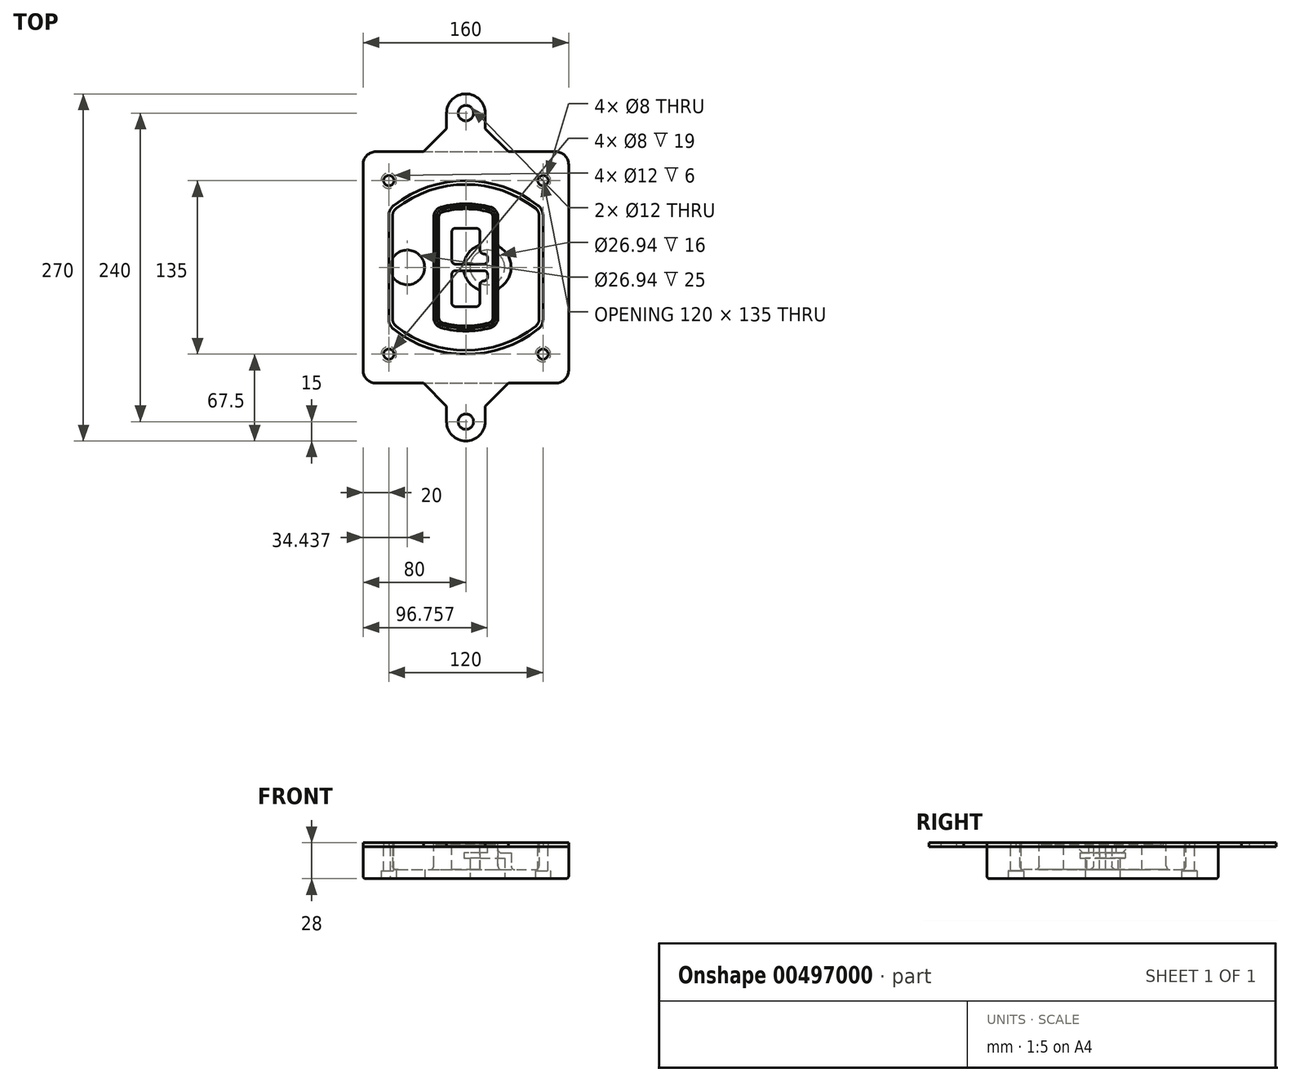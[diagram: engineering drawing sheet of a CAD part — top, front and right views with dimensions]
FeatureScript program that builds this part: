
annotation { "Feature Type Name" : "Feature", "Feature Type Description" : "" }
export const myFeature = defineFeature(function(context is Context, id is Id, definition is map)
    precondition{}
    {
        {
            var Q0;
            Q0=qCreatedBy(makeId("Top.planeOp"),FACE);
            var sketch = newSketch(context, id + "F0", { "sketchPlane" : qUnion([Q0])});
            skPoint(sketch, "E0.rect.middle", {"position": v(0, 0) * mm});
            skLineSegment(sketch, "E1.bottom", {"start": v(-70, -90) * mm, "end": v(70, -90) * mm});
            skLineSegment(sketch, "E1.top", {"start": v(-70, 90) * mm, "end": v(70, 90) * mm});
            skLineSegment(sketch, "E1.left", {"start": v(-80, -80) * mm, "end": v(-80, 80) * mm});
            skLineSegment(sketch, "E1.right", {"start": v(80, -80) * mm, "end": v(80, 80) * mm});
            skLineSegment(sketch, "E2", {"start": v(-80, 90) * mm, "end": v(80, -90) * mm, "construction": true});
            skLineSegment(sketch, "E3", {"start": v(80, 90) * mm, "end": v(-80, -90) * mm, "construction": true});
            skCircle(sketch, "E4", {"center": v(-60, 67.5) * mm, "radius": 4 * mm});
            skCircle(sketch, "E5", {"center": v(60, 67.5) * mm, "radius": 4 * mm});
            skCircle(sketch, "E6", {"center": v(60, -67.5) * mm, "radius": 4 * mm});
            skCircle(sketch, "E7", {"center": v(-60, -67.5) * mm, "radius": 4 * mm});
            skLineSegment(sketch, "E8", {"start": v(-60, 67.5) * mm, "end": v(60, 67.5) * mm, "construction": true});
            skLineSegment(sketch, "E9", {"start": v(60, 67.5) * mm, "end": v(60, -67.5) * mm, "construction": true});
            skLineSegment(sketch, "E10", {"start": v(60, -67.5) * mm, "end": v(-60, -67.5) * mm, "construction": true});
            skLineSegment(sketch, "E11", {"start": v(-60, -67.5) * mm, "end": v(-60, 67.5) * mm, "construction": true});
            skLineSegment(sketch, "E12", {"start": v(-60, 40.3) * mm, "end": v(-60, -40.3) * mm});
            skLineSegment(sketch, "E13", {"start": v(60, 40.3) * mm, "end": v(60, -40.3) * mm});
            skArc(sketch, "E14", {"start": v(56.15, 48.18) * mm, "mid": v(0, 67.5) * mm, "end": v(-56.15, 48.18) * mm});
            skArc(sketch, "E15", {"start": v(-56.15, -48.18) * mm, "mid": v(0, -67.5) * mm, "end": v(56.15, -48.18) * mm});
            skLineSegment(sketch, "E16", {"start": v(-60, 0) * mm, "end": v(60, 0) * mm, "construction": true});
            skPoint(sketch, "E17.visualSharp", {"position": v(-60, -45) * mm});
            skArc(sketch, "E17.filletArc", {"start": v(-60, -40.3) * mm, "mid": v(-58.99, -44.68) * mm, "end": v(-56.15, -48.18) * mm});
            skPoint(sketch, "E18.visualSharp", {"position": v(-60, 45) * mm});
            skArc(sketch, "E18.filletArc", {"start": v(-56.15, 48.18) * mm, "mid": v(-58.99, 44.68) * mm, "end": v(-60, 40.3) * mm});
            skPoint(sketch, "E19.visualSharp", {"position": v(60, 45) * mm});
            skArc(sketch, "E19.filletArc", {"start": v(60, 40.3) * mm, "mid": v(58.99, 44.68) * mm, "end": v(56.15, 48.18) * mm});
            skPoint(sketch, "E20.visualSharp", {"position": v(60, -45) * mm});
            skArc(sketch, "E20.filletArc", {"start": v(56.15, -48.18) * mm, "mid": v(58.99, -44.68) * mm, "end": v(60, -40.3) * mm});
            skPoint(sketch, "E21.visualSharp", {"position": v(-80, 90) * mm});
            skArc(sketch, "E21.filletArc", {"start": v(-70, 90) * mm, "mid": v(-77.07, 87.07) * mm, "end": v(-80, 80) * mm});
            skPoint(sketch, "E22.visualSharp", {"position": v(80, 90) * mm});
            skArc(sketch, "E22.filletArc", {"start": v(80, 80) * mm, "mid": v(77.07, 87.07) * mm, "end": v(70, 90) * mm});
            skPoint(sketch, "E23.visualSharp", {"position": v(80, -90) * mm});
            skArc(sketch, "E23.filletArc", {"start": v(70, -90) * mm, "mid": v(77.07, -87.07) * mm, "end": v(80, -80) * mm});
            skPoint(sketch, "E24.visualSharp", {"position": v(-80, -90) * mm});
            skArc(sketch, "E24.filletArc", {"start": v(-80, -80) * mm, "mid": v(-77.07, -87.07) * mm, "end": v(-70, -90) * mm});
            skArc(sketch, "E25.0", {"start": v(57, 40.3) * mm, "mid": v(56.3, 43.36) * mm, "end": v(54.3, 45.81) * mm});
            skLineSegment(sketch, "E25.1", {"start": v(57, 40.3) * mm, "end": v(57, -40.3) * mm});
            skArc(sketch, "E25.2", {"start": v(54.3, -45.81) * mm, "mid": v(56.3, -43.36) * mm, "end": v(57, -40.3) * mm});
            skArc(sketch, "E25.3", {"start": v(-54.3, -45.81) * mm, "mid": v(0, -64.5) * mm, "end": v(54.3, -45.81) * mm});
            skArc(sketch, "E25.4", {"start": v(-57, -40.3) * mm, "mid": v(-56.3, -43.36) * mm, "end": v(-54.3, -45.81) * mm});
            skArc(sketch, "E25.5", {"start": v(54.3, 45.81) * mm, "mid": v(0, 64.5) * mm, "end": v(-54.3, 45.81) * mm});
            skLineSegment(sketch, "E25.6", {"start": v(-57, 40.3) * mm, "end": v(-57, -40.3) * mm});
            skArc(sketch, "E25.7", {"start": v(-54.3, 45.81) * mm, "mid": v(-56.3, 43.36) * mm, "end": v(-57, 40.3) * mm});
            skArc(sketch, "E26.0", {"start": v(-58.62, 51.33) * mm, "mid": v(-62.58, 46.43) * mm, "end": v(-64, 40.3) * mm});
            skArc(sketch, "E26.1", {"start": v(58.62, 51.33) * mm, "mid": v(0, 71.5) * mm, "end": v(-58.62, 51.33) * mm});
            skArc(sketch, "E26.2", {"start": v(64, 40.3) * mm, "mid": v(62.58, 46.43) * mm, "end": v(58.62, 51.33) * mm});
            skLineSegment(sketch, "E26.3", {"start": v(64, 40.3) * mm, "end": v(64, -40.3) * mm});
            skArc(sketch, "E26.4", {"start": v(58.62, -51.33) * mm, "mid": v(62.58, -46.43) * mm, "end": v(64, -40.3) * mm});
            skLineSegment(sketch, "E26.5", {"start": v(-64, 40.3) * mm, "end": v(-64, -40.3) * mm});
            skArc(sketch, "E26.6", {"start": v(-58.62, -51.33) * mm, "mid": v(0, -71.5) * mm, "end": v(58.62, -51.33) * mm});
            skArc(sketch, "E26.7", {"start": v(-64, -40.3) * mm, "mid": v(-62.58, -46.43) * mm, "end": v(-58.62, -51.33) * mm});
            skSolve(sketch);
        }
        {
            var Q0;
            Q0=makeQuery(id+"F0.imprint","IMPRINT",FACE,{"disambiguationData":[TD([[makeQuery(id+"F0.imprint","IMPRINT",EDGE,{"derivedFrom":sQuery(id+"F0.wireOp",EDGE,"E1.bottom")}),1.0]])]});
            var Q1;
            Q1=makeQuery(id+"F0.imprint","IMPRINT",FACE,{"disambiguationData":[TD([[makeQuery(id+"F0.imprint","IMPRINT",EDGE,{"derivedFrom":sQuery(id+"F0.wireOp",EDGE,"E12")}),1.0]])]});
            var Q2;
            Q2=makeQuery(id+"F0.imprint","IMPRINT",FACE,{"disambiguationData":[TD([[makeQuery(id+"F0.imprint","IMPRINT",EDGE,{"derivedFrom":sQuery(id+"F0.wireOp",EDGE,"E25.0")}),1.0]])]});
            var Q3;
            Q3=makeQuery(id+"F0.imprint","IMPRINT",FACE,{"disambiguationData":[TD([[makeQuery(id+"F0.imprint","IMPRINT",EDGE,{"derivedFrom":sQuery(id+"F0.wireOp",EDGE,"E12")}),-1.0]])]});
            extrude(context, id + "F1", {"entities" : qUnion([Q0, Q1, Q2, Q3]), "oppositeDirection" : true, "depth" : 25 * mm});
        }
        {
            var Q0;
            Q0=makeQuery(id+"F0.imprint","IMPRINT",FACE,{"disambiguationData":[TD([[makeQuery(id+"F0.imprint","IMPRINT",EDGE,{"derivedFrom":sQuery(id+"F0.wireOp",EDGE,"E12")}),1.0]])]});
            extrude(context, id + "F2", {"entities" : qUnion([Q0]), "operationType" : NewBodyOperationType.ADD, "depth" : 3 * mm});
        }
        {
            var Q0;
            Q0=makeQuery(id+"F0.imprint","IMPRINT",FACE,{"disambiguationData":[TD([[makeQuery(id+"F0.imprint","IMPRINT",EDGE,{"derivedFrom":sQuery(id+"F0.wireOp",EDGE,"E25.0")}),1.0]])]});
            extrude(context, id + "F3", {"entities" : qUnion([Q0]), "operationType" : NewBodyOperationType.REMOVE, "oppositeDirection" : true, "depth" : 18 * mm});
        }
        {
            var Q0;
            Q0=makeQuery(id+"F2.opExtrude","CAP_FACE",FACE,{"disambiguationData":[OSD([sQuery(id+"F0.wireOp",EDGE,"E12"),sQuery(id+"F0.wireOp",EDGE,"E13"),sQuery(id+"F0.wireOp",EDGE,"E14"),sQuery(id+"F0.wireOp",EDGE,"E15"),sQuery(id+"F0.wireOp",EDGE,"E17.filletArc"),sQuery(id+"F0.wireOp",EDGE,"E18.filletArc"),sQuery(id+"F0.wireOp",EDGE,"E19.filletArc"),sQuery(id+"F0.wireOp",EDGE,"E20.filletArc"),sQuery(id+"F0.wireOp",EDGE,"E25.0"),sQuery(id+"F0.wireOp",EDGE,"E25.1"),sQuery(id+"F0.wireOp",EDGE,"E25.2"),sQuery(id+"F0.wireOp",EDGE,"E25.3"),sQuery(id+"F0.wireOp",EDGE,"E25.4"),sQuery(id+"F0.wireOp",EDGE,"E25.5"),sQuery(id+"F0.wireOp",EDGE,"E25.6"),sQuery(id+"F0.wireOp",EDGE,"E25.7")])],"isStart":false});
            var sketch = newSketch(context, id + "F4", { "sketchPlane" : qUnion([Q0])});
            skArc(sketch, "E27.0", {"start": v(-19.08, -46.97) * mm, "mid": v(0, -49.5) * mm, "end": v(19.08, -46.97) * mm});
            skArc(sketch, "E28.0", {"start": v(19.08, 46.97) * mm, "mid": v(0, 49.5) * mm, "end": v(-19.08, 46.97) * mm});
            skLineSegment(sketch, "E29", {"start": v(-25, 39.25) * mm, "end": v(-25, -39.25) * mm});
            skLineSegment(sketch, "E30", {"start": v(25, 39.25) * mm, "end": v(25, -39.25) * mm});
            skLineSegment(sketch, "E31", {"start": v(-25, 45.1) * mm, "end": v(25, 45.1) * mm, "construction": true});
            skLineSegment(sketch, "E32", {"start": v(-25, -45.1) * mm, "end": v(25, -45.1) * mm, "construction": true});
            skPoint(sketch, "E33.visualSharp", {"position": v(-25, 45.1) * mm});
            skArc(sketch, "E33.filletArc", {"start": v(-19.08, 46.97) * mm, "mid": v(-23.35, 44.11) * mm, "end": v(-25, 39.25) * mm});
            skPoint(sketch, "E34.visualSharp", {"position": v(25, 45.1) * mm});
            skArc(sketch, "E34.filletArc", {"start": v(25, 39.25) * mm, "mid": v(23.35, 44.11) * mm, "end": v(19.08, 46.97) * mm});
            skPoint(sketch, "E35.visualSharp", {"position": v(25, -45.1) * mm});
            skArc(sketch, "E35.filletArc", {"start": v(19.08, -46.97) * mm, "mid": v(23.35, -44.11) * mm, "end": v(25, -39.25) * mm});
            skPoint(sketch, "E36.visualSharp", {"position": v(-25, -45.1) * mm});
            skArc(sketch, "E36.filletArc", {"start": v(-25, -39.25) * mm, "mid": v(-23.35, -44.11) * mm, "end": v(-19.08, -46.97) * mm});
            skArc(sketch, "E37.0", {"start": v(54.3, 45.81) * mm, "mid": v(0, 64.5) * mm, "end": v(-54.3, 45.81) * mm});
            skArc(sketch, "E37.1", {"start": v(-54.3, 45.81) * mm, "mid": v(-56.3, 43.36) * mm, "end": v(-57, 40.3) * mm});
            skLineSegment(sketch, "E37.2", {"start": v(-57, 40.3) * mm, "end": v(-57, -40.3) * mm});
            skArc(sketch, "E37.3", {"start": v(-57, -40.3) * mm, "mid": v(-56.3, -43.36) * mm, "end": v(-54.3, -45.81) * mm});
            skArc(sketch, "E37.4", {"start": v(-54.3, -45.81) * mm, "mid": v(0, -64.5) * mm, "end": v(54.3, -45.81) * mm});
            skArc(sketch, "E37.5", {"start": v(54.3, -45.81) * mm, "mid": v(56.3, -43.36) * mm, "end": v(57, -40.3) * mm});
            skLineSegment(sketch, "E37.6", {"start": v(57, 40.3) * mm, "end": v(57, -40.3) * mm});
            skArc(sketch, "E37.7", {"start": v(57, 40.3) * mm, "mid": v(56.3, 43.36) * mm, "end": v(54.3, 45.81) * mm});
            skLineSegment(sketch, "E38.0", {"start": v(23, 39.25) * mm, "end": v(23, -39.25) * mm});
            skArc(sketch, "E38.1", {"start": v(18.56, -45.04) * mm, "mid": v(21.76, -42.9) * mm, "end": v(23, -39.25) * mm});
            skArc(sketch, "E38.2", {"start": v(-18.56, -45.04) * mm, "mid": v(0, -47.5) * mm, "end": v(18.56, -45.04) * mm});
            skArc(sketch, "E38.3", {"start": v(-23, -39.25) * mm, "mid": v(-21.76, -42.9) * mm, "end": v(-18.56, -45.04) * mm});
            skLineSegment(sketch, "E38.4", {"start": v(-23, 39.25) * mm, "end": v(-23, -39.25) * mm});
            skArc(sketch, "E38.5", {"start": v(23, 39.25) * mm, "mid": v(21.76, 42.9) * mm, "end": v(18.56, 45.04) * mm});
            skArc(sketch, "E38.6", {"start": v(-18.56, 45.04) * mm, "mid": v(-21.76, 42.9) * mm, "end": v(-23, 39.25) * mm});
            skArc(sketch, "E38.7", {"start": v(18.56, 45.04) * mm, "mid": v(0, 47.5) * mm, "end": v(-18.56, 45.04) * mm});
            skArc(sketch, "E39.0", {"start": v(21, 39.25) * mm, "mid": v(20.18, 41.68) * mm, "end": v(18.04, 43.1) * mm});
            skLineSegment(sketch, "E39.1", {"start": v(21, 39.25) * mm, "end": v(21, -39.25) * mm});
            skArc(sketch, "E39.2", {"start": v(18.04, -43.1) * mm, "mid": v(20.18, -41.68) * mm, "end": v(21, -39.25) * mm});
            skArc(sketch, "E39.3", {"start": v(-18.04, -43.1) * mm, "mid": v(0, -45.5) * mm, "end": v(18.04, -43.1) * mm});
            skArc(sketch, "E39.4", {"start": v(-21, -39.25) * mm, "mid": v(-20.18, -41.68) * mm, "end": v(-18.04, -43.1) * mm});
            skArc(sketch, "E39.5", {"start": v(18.04, 43.1) * mm, "mid": v(0, 45.5) * mm, "end": v(-18.04, 43.1) * mm});
            skLineSegment(sketch, "E39.6", {"start": v(-21, 39.25) * mm, "end": v(-21, -39.25) * mm});
            skArc(sketch, "E39.7", {"start": v(-18.04, 43.1) * mm, "mid": v(-20.18, 41.68) * mm, "end": v(-21, 39.25) * mm});
            skLineSegment(sketch, "E40", {"start": v(-25, 0) * mm, "end": v(25, 0) * mm, "construction": true});
            skLineSegment(sketch, "E41", {"start": v(-11, 5.5) * mm, "end": v(-11, 27.5) * mm});
            skLineSegment(sketch, "E42", {"start": v(-8, 30.5) * mm, "end": v(8, 30.5) * mm});
            skLineSegment(sketch, "E43", {"start": v(11, 27.5) * mm, "end": v(11, 13.5) * mm});
            skLineSegment(sketch, "E44", {"start": v(14, 10.5) * mm, "end": v(14, 10.5) * mm});
            skLineSegment(sketch, "E45", {"start": v(17, 7.5) * mm, "end": v(17, 5.5) * mm});
            skLineSegment(sketch, "E46", {"start": v(14, 2.5) * mm, "end": v(-8, 2.5) * mm});
            skPoint(sketch, "E47.visualSharp", {"position": v(-11, 30.5) * mm});
            skArc(sketch, "E47.filletArc", {"start": v(-8, 30.5) * mm, "mid": v(-10.12, 29.62) * mm, "end": v(-11, 27.5) * mm});
            skPoint(sketch, "E48.visualSharp", {"position": v(11, 30.5) * mm});
            skArc(sketch, "E48.filletArc", {"start": v(11, 27.5) * mm, "mid": v(10.12, 29.62) * mm, "end": v(8, 30.5) * mm});
            skPoint(sketch, "E49.visualSharp", {"position": v(11, 10.5) * mm});
            skArc(sketch, "E49.filletArc", {"start": v(11, 13.5) * mm, "mid": v(11.88, 11.38) * mm, "end": v(14, 10.5) * mm});
            skPoint(sketch, "E50.visualSharp", {"position": v(17, 10.5) * mm});
            skArc(sketch, "E50.filletArc", {"start": v(17, 7.5) * mm, "mid": v(16.12, 9.62) * mm, "end": v(14, 10.5) * mm});
            skPoint(sketch, "E51.visualSharp", {"position": v(17, 2.5) * mm});
            skArc(sketch, "E51.filletArc", {"start": v(14, 2.5) * mm, "mid": v(16.12, 3.38) * mm, "end": v(17, 5.5) * mm});
            skPoint(sketch, "E52.visualSharp", {"position": v(-11, 2.5) * mm});
            skArc(sketch, "E52.filletArc", {"start": v(-11, 5.5) * mm, "mid": v(-10.12, 3.38) * mm, "end": v(-8, 2.5) * mm});
            skLineSegment(sketch, "E53.0.MirrorCS", {"start": v(14, -2.5) * mm, "end": v(-8, -2.5) * mm});
            skArc(sketch, "E54.0.MirrorCS", {"start": v(-11, -5.5) * mm, "mid": v(-10.12, -3.38) * mm, "end": v(-8, -2.5) * mm});
            skLineSegment(sketch, "E55.0.MirrorCS", {"start": v(-11, -5.5) * mm, "end": v(-11, -27.5) * mm});
            skArc(sketch, "E56.0.MirrorCS", {"start": v(-8, -30.5) * mm, "mid": v(-10.12, -29.62) * mm, "end": v(-11, -27.5) * mm});
            skLineSegment(sketch, "E57.0.MirrorCS", {"start": v(-8, -30.5) * mm, "end": v(8, -30.5) * mm});
            skArc(sketch, "E58.0.MirrorCS", {"start": v(11, -27.5) * mm, "mid": v(10.12, -29.62) * mm, "end": v(8, -30.5) * mm});
            skLineSegment(sketch, "E59.0.MirrorCS", {"start": v(11, -27.5) * mm, "end": v(11, -13.5) * mm});
            skArc(sketch, "E60.0.MirrorCS", {"start": v(11, -13.5) * mm, "mid": v(11.88, -11.38) * mm, "end": v(14, -10.5) * mm});
            skArc(sketch, "E61.0.MirrorCS", {"start": v(17, -7.5) * mm, "mid": v(16.12, -9.62) * mm, "end": v(14, -10.5) * mm});
            skLineSegment(sketch, "E62.0.MirrorCS", {"start": v(17, -7.5) * mm, "end": v(17, -5.5) * mm});
            skArc(sketch, "E63.0.MirrorCS", {"start": v(14, -2.5) * mm, "mid": v(16.12, -3.38) * mm, "end": v(17, -5.5) * mm});
            skSolve(sketch);
        }
        {
            var Q0;
            Q0=makeQuery(id+"F4.imprint","IMPRINT",FACE,{"disambiguationData":[TD([[makeQuery(id+"F4.imprint","IMPRINT",EDGE,{"derivedFrom":sQuery(id+"F4.wireOp",EDGE,"E27.0")}),1.0]])]});
            var Q1;
            Q1=makeQuery(id+"F4.imprint","IMPRINT",FACE,{"disambiguationData":[TD([[makeQuery(id+"F4.imprint","IMPRINT",EDGE,{"derivedFrom":sQuery(id+"F4.wireOp",EDGE,"E38.0")}),-1.0]])]});
            var Q2;
            Q2=makeQuery(id+"F4.imprint","IMPRINT",FACE,{"disambiguationData":[TD([[makeQuery(id+"F4.imprint","IMPRINT",EDGE,{"derivedFrom":sQuery(id+"F4.wireOp",EDGE,"E39.0")}),1.0]])]});
            extrude(context, id + "F5", {"entities" : qUnion([Q0, Q1, Q2]), "operationType" : NewBodyOperationType.ADD, "endBound" : BoundingType.UP_TO_NEXT, "oppositeDirection" : true, "depth" : 25 * mm});
        }
        {
            var Q0;
            Q0=makeQuery(id+"F4.imprint","IMPRINT",FACE,{"disambiguationData":[TD([[makeQuery(id+"F4.imprint","IMPRINT",EDGE,{"derivedFrom":sQuery(id+"F4.wireOp",EDGE,"E38.0")}),-1.0]])]});
            extrude(context, id + "F6", {"entities" : qUnion([Q0]), "operationType" : NewBodyOperationType.REMOVE, "oppositeDirection" : true, "depth" : 2 * mm});
        }
        {
            var Q0;
            Q0=makeQuery(id+"F1.opExtrude","CAP_FACE",FACE,{"disambiguationData":[OSD([sQuery(id+"F0.wireOp",EDGE,"E1.bottom"),sQuery(id+"F0.wireOp",EDGE,"E1.top"),sQuery(id+"F0.wireOp",EDGE,"E1.left"),sQuery(id+"F0.wireOp",EDGE,"E1.right"),sQuery(id+"F0.wireOp",EDGE,"E4"),sQuery(id+"F0.wireOp",EDGE,"E5"),sQuery(id+"F0.wireOp",EDGE,"E6"),sQuery(id+"F0.wireOp",EDGE,"E7"),sQuery(id+"F0.wireOp",EDGE,"E21.filletArc"),sQuery(id+"F0.wireOp",EDGE,"E22.filletArc"),sQuery(id+"F0.wireOp",EDGE,"E23.filletArc"),sQuery(id+"F0.wireOp",EDGE,"E24.filletArc")])],"isStart":false});
            var sketch = newSketch(context, id + "F7", { "sketchPlane" : qUnion([Q0])});
            skCircle(sketch, "E64", {"center": v(16.76, 0) * mm, "radius": 13.47 * mm});
            skCircle(sketch, "E65", {"center": v(-45.56, 0) * mm, "radius": 13.47 * mm});
            skLineSegment(sketch, "E66", {"start": v(80, 0) * mm, "end": v(-80, 0) * mm});
            skCircle(sketch, "E67", {"center": v(16.76, 0) * mm, "radius": 18.47 * mm});
            skCircle(sketch, "E68", {"center": v(60, -67.5) * mm, "radius": 6 * mm});
            skCircle(sketch, "E69", {"center": v(-60, -67.5) * mm, "radius": 6 * mm});
            skCircle(sketch, "E70", {"center": v(-60, 67.5) * mm, "radius": 6 * mm});
            skCircle(sketch, "E71", {"center": v(60, 67.5) * mm, "radius": 6 * mm});
            skSolve(sketch);
        }
        {
            var Q0;
            {var subQ1=sQuery(id+"F7.wireOp",EDGE,"E66");var subQ4=sQuery(id+"F7.wireOp",EDGE,"E64");var subQ6=makeQuery(id+"F7.imprint","INTERSECT",VERTEX,{"disambiguationData":[OD(0.0)],"derivedFrom":[subQ4,subQ1]});Q0=makeQuery(id+"F7.imprint","IMPRINT",FACE,{"disambiguationData":[TD([[makeQuery(id+"F7.imprint","IMPRINT",EDGE,{"disambiguationData":[TD([[subQ6,-1.0]])],"derivedFrom":subQ4}),-1.0]])]});}
            var Q1;
            {var subQ0=sQuery(id+"F7.wireOp",EDGE,"E66");var subQ1=sQuery(id+"F7.wireOp",EDGE,"E64");var subQ3=makeQuery(id+"F7.imprint","INTERSECT",VERTEX,{"disambiguationData":[OD(0.0)],"derivedFrom":[subQ1,subQ0]});Q1=makeQuery(id+"F7.imprint","IMPRINT",FACE,{"disambiguationData":[TD([[makeQuery(id+"F7.imprint","IMPRINT",EDGE,{"disambiguationData":[TD([[subQ3,-1.0]])],"derivedFrom":subQ1}),1.0]])]});}
            var Q2;
            {var subQ0=sQuery(id+"F7.wireOp",EDGE,"E66");var subQ1=sQuery(id+"F7.wireOp",EDGE,"E64");var subQ3=makeQuery(id+"F7.imprint","INTERSECT",VERTEX,{"disambiguationData":[OD(0.0)],"derivedFrom":[subQ1,subQ0]});Q2=makeQuery(id+"F7.imprint","IMPRINT",FACE,{"disambiguationData":[TD([[makeQuery(id+"F7.imprint","IMPRINT",EDGE,{"disambiguationData":[TD([[subQ3,1.0]])],"derivedFrom":subQ1}),1.0]])]});}
            var Q3;
            {var subQ1=sQuery(id+"F7.wireOp",EDGE,"E66");var subQ4=sQuery(id+"F7.wireOp",EDGE,"E64");var subQ6=makeQuery(id+"F7.imprint","INTERSECT",VERTEX,{"disambiguationData":[OD(0.0)],"derivedFrom":[subQ4,subQ1]});Q3=makeQuery(id+"F7.imprint","IMPRINT",FACE,{"disambiguationData":[TD([[makeQuery(id+"F7.imprint","IMPRINT",EDGE,{"disambiguationData":[TD([[subQ6,1.0]])],"derivedFrom":subQ4}),-1.0]])]});}
            extrude(context, id + "F8", {"entities" : qUnion([Q0, Q1, Q2, Q3]), "operationType" : NewBodyOperationType.ADD, "oppositeDirection" : true, "depth" : 20 * mm});
        }
        {
            var Q0;
            {var subQ0=sQuery(id+"F7.wireOp",EDGE,"E66");var subQ1=sQuery(id+"F7.wireOp",EDGE,"E64");var subQ3=makeQuery(id+"F7.imprint","INTERSECT",VERTEX,{"disambiguationData":[OD(0.0)],"derivedFrom":[subQ1,subQ0]});Q0=makeQuery(id+"F7.imprint","IMPRINT",FACE,{"disambiguationData":[TD([[makeQuery(id+"F7.imprint","IMPRINT",EDGE,{"disambiguationData":[TD([[subQ3,-1.0]])],"derivedFrom":subQ1}),1.0]])]});}
            var Q1;
            {var subQ0=sQuery(id+"F7.wireOp",EDGE,"E66");var subQ1=sQuery(id+"F7.wireOp",EDGE,"E64");var subQ3=makeQuery(id+"F7.imprint","INTERSECT",VERTEX,{"disambiguationData":[OD(0.0)],"derivedFrom":[subQ1,subQ0]});Q1=makeQuery(id+"F7.imprint","IMPRINT",FACE,{"disambiguationData":[TD([[makeQuery(id+"F7.imprint","IMPRINT",EDGE,{"disambiguationData":[TD([[subQ3,1.0]])],"derivedFrom":subQ1}),1.0]])]});}
            extrude(context, id + "F9", {"entities" : qUnion([Q0, Q1]), "operationType" : NewBodyOperationType.REMOVE, "oppositeDirection" : true, "depth" : 16 * mm});
        }
        {
            var Q0;
            {var subQ0=sQuery(id+"F7.wireOp",EDGE,"E66");var subQ1=sQuery(id+"F7.wireOp",EDGE,"E65");var subQ3=makeQuery(id+"F7.imprint","INTERSECT",VERTEX,{"disambiguationData":[OD(0.0)],"derivedFrom":[subQ1,subQ0]});Q0=makeQuery(id+"F7.imprint","IMPRINT",FACE,{"disambiguationData":[TD([[makeQuery(id+"F7.imprint","IMPRINT",EDGE,{"disambiguationData":[TD([[subQ3,-1.0]])],"derivedFrom":subQ1}),1.0]])]});}
            var Q1;
            {var subQ0=sQuery(id+"F7.wireOp",EDGE,"E66");var subQ1=sQuery(id+"F7.wireOp",EDGE,"E65");var subQ3=makeQuery(id+"F7.imprint","INTERSECT",VERTEX,{"disambiguationData":[OD(0.0)],"derivedFrom":[subQ1,subQ0]});Q1=makeQuery(id+"F7.imprint","IMPRINT",FACE,{"disambiguationData":[TD([[makeQuery(id+"F7.imprint","IMPRINT",EDGE,{"disambiguationData":[TD([[subQ3,1.0]])],"derivedFrom":subQ1}),1.0]])]});}
            extrude(context, id + "F10", {"entities" : qUnion([Q0, Q1]), "operationType" : NewBodyOperationType.REMOVE, "oppositeDirection" : true, "depth" : 25 * mm});
        }
        {
            var Q0;
            Q0=makeQuery(id+"F7.imprint","IMPRINT",FACE,{"disambiguationData":[TD([[makeQuery(id+"F7.imprint","IMPRINT",EDGE,{"derivedFrom":sQuery(id+"F7.wireOp",EDGE,"E68")}),1.0]])]});
            var Q1;
            Q1=makeQuery(id+"F7.imprint","IMPRINT",FACE,{"disambiguationData":[TD([[makeQuery(id+"F7.imprint","IMPRINT",EDGE,{"derivedFrom":makeQuery(id+"F1.opExtrude","CAP_EDGE",EDGE,{"disambiguationData":[OSD([sQuery(id+"F0.wireOp",EDGE,"E5")])],"isStart":false})}),-1.0]])]});
            var Q2;
            Q2=makeQuery(id+"F7.imprint","IMPRINT",FACE,{"disambiguationData":[TD([[makeQuery(id+"F7.imprint","IMPRINT",EDGE,{"derivedFrom":sQuery(id+"F7.wireOp",EDGE,"E69")}),1.0]])]});
            var Q3;
            Q3=makeQuery(id+"F7.imprint","IMPRINT",FACE,{"disambiguationData":[TD([[makeQuery(id+"F7.imprint","IMPRINT",EDGE,{"derivedFrom":makeQuery(id+"F1.opExtrude","CAP_EDGE",EDGE,{"disambiguationData":[OSD([sQuery(id+"F0.wireOp",EDGE,"E4")])],"isStart":false})}),-1.0]])]});
            var Q4;
            Q4=makeQuery(id+"F7.imprint","IMPRINT",FACE,{"disambiguationData":[TD([[makeQuery(id+"F7.imprint","IMPRINT",EDGE,{"derivedFrom":sQuery(id+"F7.wireOp",EDGE,"E70")}),1.0]])]});
            var Q5;
            Q5=makeQuery(id+"F7.imprint","IMPRINT",FACE,{"disambiguationData":[TD([[makeQuery(id+"F7.imprint","IMPRINT",EDGE,{"derivedFrom":makeQuery(id+"F1.opExtrude","CAP_EDGE",EDGE,{"disambiguationData":[OSD([sQuery(id+"F0.wireOp",EDGE,"E7")])],"isStart":false})}),-1.0]])]});
            var Q6;
            Q6=makeQuery(id+"F7.imprint","IMPRINT",FACE,{"disambiguationData":[TD([[makeQuery(id+"F7.imprint","IMPRINT",EDGE,{"derivedFrom":sQuery(id+"F7.wireOp",EDGE,"E71")}),1.0]])]});
            var Q7;
            Q7=makeQuery(id+"F7.imprint","IMPRINT",FACE,{"disambiguationData":[TD([[makeQuery(id+"F7.imprint","IMPRINT",EDGE,{"derivedFrom":makeQuery(id+"F1.opExtrude","CAP_EDGE",EDGE,{"disambiguationData":[OSD([sQuery(id+"F0.wireOp",EDGE,"E6")])],"isStart":false})}),-1.0]])]});
            extrude(context, id + "F11", {"entities" : qUnion([Q0, Q1, Q2, Q3, Q4, Q5, Q6, Q7]), "operationType" : NewBodyOperationType.REMOVE, "oppositeDirection" : true, "depth" : 6 * mm});
        }
        {
            var Q0;
            Q0=makeQuery(id+"F9.boolean.opBoolean","COPY",FACE,{"derivedFrom":makeQuery(id+"F9.opExtrude","CAP_FACE",FACE,{"disambiguationData":[OSD([sQuery(id+"F7.wireOp",EDGE,"E64")])],"isStart":false})});
            var sketch = newSketch(context, id + "F12", { "sketchPlane" : qUnion([Q0])});
            skArc(sketch, "E72.0", {"start": v(11, 17.55) * mm, "mid": v(2.57, 11.82) * mm, "end": v(-1.54, 2.5) * mm});
            skArc(sketch, "E72.1", {"start": v(-1.54, -2.5) * mm, "mid": v(2.57, -11.82) * mm, "end": v(11, -17.55) * mm});
            skLineSegment(sketch, "E73", {"start": v(-1.54, -2.5) * mm, "end": v(14, -2.5) * mm});
            skLineSegment(sketch, "E74.0", {"start": v(14, 2.5) * mm, "end": v(-1.54, 2.5) * mm});
            skArc(sketch, "E74.1", {"start": v(14, 2.5) * mm, "mid": v(16.12, 3.38) * mm, "end": v(17, 5.5) * mm});
            skLineSegment(sketch, "E74.2", {"start": v(17, 7.5) * mm, "end": v(17, 5.5) * mm});
            skArc(sketch, "E74.3", {"start": v(17, 7.5) * mm, "mid": v(16.12, 9.62) * mm, "end": v(14, 10.5) * mm});
            skArc(sketch, "E74.4", {"start": v(11, 13.5) * mm, "mid": v(11.88, 11.38) * mm, "end": v(14, 10.5) * mm});
            skLineSegment(sketch, "E74.5", {"start": v(11, 17.55) * mm, "end": v(11, 13.5) * mm});
            skLineSegment(sketch, "E74.7", {"start": v(14, -2.5) * mm, "end": v(-1.54, -2.5) * mm});
            skArc(sketch, "E74.8", {"start": v(14, -2.5) * mm, "mid": v(16.12, -3.38) * mm, "end": v(17, -5.5) * mm});
            skLineSegment(sketch, "E74.9", {"start": v(17, -7.5) * mm, "end": v(17, -5.5) * mm});
            skArc(sketch, "E74.10", {"start": v(17, -7.5) * mm, "mid": v(16.12, -9.62) * mm, "end": v(14, -10.5) * mm});
            skArc(sketch, "E74.11", {"start": v(11, -13.5) * mm, "mid": v(11.88, -11.38) * mm, "end": v(14, -10.5) * mm});
            skLineSegment(sketch, "E74.12", {"start": v(11, -17.55) * mm, "end": v(11, -13.5) * mm});
            skPoint(sketch, "E75.orphan", {"position": v(11, -27.5) * mm});
            skPoint(sketch, "E76.orphan", {"position": v(-8, -2.5) * mm});
            skPoint(sketch, "E77.orphan", {"position": v(-8, 2.5) * mm});
            skPoint(sketch, "E78.orphan", {"position": v(11, 27.5) * mm});
            skSolve(sketch);
        }
        {
            var Q0;
            {var subQ7=sQuery(id+"F12.wireOp",EDGE,"E72.0");var subQ14=sQuery(id+"F12.wireOp",EDGE,"E72.1");var subQ16=sQuery(id+"F12.wireOp",EDGE,"E74.1");var subQ18=sQuery(id+"F12.wireOp",EDGE,"E74.8");Q0=qUnion([makeQuery(id+"F12.imprint","IMPRINT",FACE,{"disambiguationData":[TD([[makeQuery(id+"F12.imprint","IMPRINT",EDGE,{"derivedFrom":subQ7}),1.0]])]}),makeQuery(id+"F12.imprint","IMPRINT",FACE,{"disambiguationData":[TD([[makeQuery(id+"F12.imprint","IMPRINT",EDGE,{"derivedFrom":subQ14}),1.0]])]}),makeQuery(id+"F12.imprint","IMPRINT",FACE,{"disambiguationData":[TD([[makeQuery(id+"F12.imprint","IMPRINT",EDGE,{"derivedFrom":subQ16}),1.0]])]}),makeQuery(id+"F12.imprint","IMPRINT",FACE,{"disambiguationData":[TD([[makeQuery(id+"F12.imprint","IMPRINT",EDGE,{"derivedFrom":subQ18}),-1.0]])]})]);}
            var Q1;
            Q1=makeQuery(id+"F5.boolean.opBoolean","SPLIT",FACE,{"disambiguationData":[TD([makeQuery(id+"F5.opExtrude","SWEPT_FACE",FACE,{"disambiguationData":[OSD([sQuery(id+"F4.wireOp",EDGE,"E41")])]})])],"derivedFrom":makeQuery(id+"F3.boolean.opBoolean","COPY",FACE,{"derivedFrom":makeQuery(id+"F3.opExtrude","CAP_FACE",FACE,{"disambiguationData":[OSD([sQuery(id+"F0.wireOp",EDGE,"E25.0"),sQuery(id+"F0.wireOp",EDGE,"E25.1"),sQuery(id+"F0.wireOp",EDGE,"E25.2"),sQuery(id+"F0.wireOp",EDGE,"E25.3"),sQuery(id+"F0.wireOp",EDGE,"E25.4"),sQuery(id+"F0.wireOp",EDGE,"E25.5"),sQuery(id+"F0.wireOp",EDGE,"E25.6"),sQuery(id+"F0.wireOp",EDGE,"E25.7")])],"isStart":false})})});
            extrude(context, id + "F13", {"entities" : qUnion([Q0]), "operationType" : NewBodyOperationType.REMOVE, "endBound" : BoundingType.UP_TO_SURFACE, "endBoundEntityFace" : qUnion([Q1]), "depth" : 25 * mm});
        }
        {
            var Q0;
            Q0=makeQuery(id+"F3.boolean.opBoolean","COPY",EDGE,{"derivedFrom":makeQuery(id+"F3.opExtrude","CAP_EDGE",EDGE,{"disambiguationData":[OSD([sQuery(id+"F0.wireOp",EDGE,"E25.6")])],"isStart":false})});
            var Q1;
            Q1=makeQuery(id+"F8.boolean.opBoolean","INTERSECT",EDGE,{"derivedFrom":[makeQuery(id+"F5.opExtrude","SWEPT_FACE",FACE,{"disambiguationData":[OSD([sQuery(id+"F4.wireOp",EDGE,"E30")])]}),makeQuery(id+"F8.opExtrude","CAP_FACE",FACE,{"disambiguationData":[OSD([sQuery(id+"F7.wireOp",EDGE,"E67")])],"isStart":false})]});
            var Q2;
            Q2=makeQuery(id+"F8.boolean.opBoolean","INTERSECT",EDGE,{"disambiguationData":[OD(1.0)],"derivedFrom":[makeQuery(id+"F5.opExtrude","SWEPT_FACE",FACE,{"disambiguationData":[OSD([sQuery(id+"F4.wireOp",EDGE,"E30")])]}),makeQuery(id+"F8.opExtrude","SWEPT_FACE",FACE,{"disambiguationData":[OSD([sQuery(id+"F7.wireOp",EDGE,"E67")])]})]});
            var Q3;
            {var subQ0=sQuery(id+"F4.wireOp",EDGE,"E30");Q3=makeQuery(id+"F8.boolean.opBoolean","SPLIT",EDGE,{"disambiguationData":[TD([makeQuery(id+"F5.opExtrude","SWEPT_FACE",FACE,{"disambiguationData":[OSD([sQuery(id+"F4.wireOp",EDGE,"E35.filletArc")])]})])],"derivedFrom":makeQuery(id+"F5.opExtrude","CAP_EDGE",EDGE,{"disambiguationData":[OSD([subQ0])],"isStart":false})});}
            var Q4;
            {var subQ0=sQuery(id+"F0.wireOp",EDGE,"E25.7");var subQ1=sQuery(id+"F0.wireOp",EDGE,"E25.1");var subQ2=sQuery(id+"F0.wireOp",EDGE,"E25.6");var subQ3=sQuery(id+"F0.wireOp",EDGE,"E25.5");var subQ4=sQuery(id+"F0.wireOp",EDGE,"E25.4");var subQ5=sQuery(id+"F0.wireOp",EDGE,"E25.0");var subQ6=sQuery(id+"F0.wireOp",EDGE,"E25.2");var subQ7=sQuery(id+"F0.wireOp",EDGE,"E25.3");Q4=makeQuery(id+"F8.boolean.opBoolean","INTERSECT",EDGE,{"derivedFrom":[makeQuery(id+"F5.boolean.opBoolean","SPLIT",FACE,{"disambiguationData":[TD([makeQuery(id+"F2.opExtrude","SWEPT_FACE",FACE,{"disambiguationData":[OSD([subQ5])]})])],"derivedFrom":makeQuery(id+"F3.boolean.opBoolean","COPY",FACE,{"derivedFrom":makeQuery(id+"F3.opExtrude","CAP_FACE",FACE,{"disambiguationData":[OSD([subQ5,subQ1,subQ6,subQ7,subQ4,subQ3,subQ2,subQ0])],"isStart":false})})}),makeQuery(id+"F8.opExtrude","SWEPT_FACE",FACE,{"disambiguationData":[OSD([sQuery(id+"F7.wireOp",EDGE,"E67")])]})]});}
            var Q5;
            Q5=makeQuery(id+"F8.boolean.opBoolean","INTERSECT",EDGE,{"disambiguationData":[OD(0.0)],"derivedFrom":[makeQuery(id+"F5.opExtrude","SWEPT_FACE",FACE,{"disambiguationData":[OSD([sQuery(id+"F4.wireOp",EDGE,"E30")])]}),makeQuery(id+"F8.opExtrude","SWEPT_FACE",FACE,{"disambiguationData":[OSD([sQuery(id+"F7.wireOp",EDGE,"E67")])]})]});
            fillet(context, id + "F14", {"entities" : qUnion([Q0, Q1, Q2, Q3, Q4, Q5]), "radius" : 3 * mm, "tangentPropagation" : true, "allowEdgeOverflow" : false});
        }
        {
            var Q0;
            Q0=makeQuery(id+"F1.opExtrude","CAP_EDGE",EDGE,{"disambiguationData":[OSD([sQuery(id+"F0.wireOp",EDGE,"E1.bottom")])],"isStart":false});
            fillet(context, id + "F15", {"entities" : qUnion([Q0]), "radius" : 2 * mm, "tangentPropagation" : true, "allowEdgeOverflow" : false});
        }
        {
            var Q0;
            {var subQ0=sQuery(id+"F0.wireOp",EDGE,"E21.filletArc");var subQ1=sQuery(id+"F0.wireOp",EDGE,"E7");var subQ2=sQuery(id+"F0.wireOp",EDGE,"E6");var subQ3=sQuery(id+"F0.wireOp",EDGE,"E5");var subQ4=sQuery(id+"F0.wireOp",EDGE,"E4");var subQ5=sQuery(id+"F0.wireOp",EDGE,"E22.filletArc");var subQ6=sQuery(id+"F0.wireOp",EDGE,"E1.bottom");var subQ7=sQuery(id+"F0.wireOp",EDGE,"E1.right");var subQ8=sQuery(id+"F0.wireOp",EDGE,"E1.top");var subQ9=sQuery(id+"F0.wireOp",EDGE,"E1.left");var subQ10=sQuery(id+"F0.wireOp",EDGE,"E23.filletArc");var subQ11=sQuery(id+"F0.wireOp",EDGE,"E24.filletArc");Q0=makeQuery(id+"F2.boolean.opBoolean","SPLIT",FACE,{"disambiguationData":[TD([makeQuery(id+"F1.opExtrude","SWEPT_FACE",FACE,{"disambiguationData":[OSD([subQ6])]})])],"derivedFrom":makeQuery(id+"F1.opExtrude","CAP_FACE",FACE,{"disambiguationData":[OSD([subQ6,subQ8,subQ9,subQ7,subQ4,subQ3,subQ2,subQ1,subQ0,subQ5,subQ10,subQ11])],"isStart":true})});}
            var sketch = newSketch(context, id + "F16", { "sketchPlane" : qUnion([Q0])});
            skLineSegment(sketch, "E79", {"start": v(0, 90) * mm, "end": v(0, 120) * mm, "construction": true});
            skCircle(sketch, "E80", {"center": v(0, 120) * mm, "radius": 6 * mm});
            skLineSegment(sketch, "E81", {"start": v(0, -90) * mm, "end": v(0, -120) * mm, "construction": true});
            skCircle(sketch, "E82", {"center": v(0, -120) * mm, "radius": 6 * mm});
            skLineSegment(sketch, "E83", {"start": v(0, 120) * mm, "end": v(-15, 120) * mm, "construction": true});
            skLineSegment(sketch, "E84", {"start": v(0, 120) * mm, "end": v(15, 120) * mm, "construction": true});
            skLineSegment(sketch, "E85", {"start": v(0, -120) * mm, "end": v(15, -120) * mm, "construction": true});
            skLineSegment(sketch, "E86", {"start": v(0, -120) * mm, "end": v(-15, -120) * mm, "construction": true});
            skLineSegment(sketch, "E87", {"start": v(-15, 120) * mm, "end": v(-15, 108) * mm});
            skLineSegment(sketch, "E88", {"start": v(15, 120) * mm, "end": v(15, 108) * mm});
            skLineSegment(sketch, "E89", {"start": v(-15, -120) * mm, "end": v(-15, -108) * mm});
            skLineSegment(sketch, "E90", {"start": v(15, -120) * mm, "end": v(15, -108) * mm});
            skArc(sketch, "E91", {"start": v(15, 120) * mm, "mid": v(0, 135) * mm, "end": v(-15, 120) * mm});
            skArc(sketch, "E92", {"start": v(-15, -120) * mm, "mid": v(0, -135) * mm, "end": v(15, -120) * mm});
            skLineSegment(sketch, "E93", {"start": v(-15, 108) * mm, "end": v(-33, 90) * mm});
            skLineSegment(sketch, "E94", {"start": v(15, 108) * mm, "end": v(33, 90) * mm});
            skLineSegment(sketch, "E95", {"start": v(15, -108) * mm, "end": v(33, -90) * mm});
            skLineSegment(sketch, "E96", {"start": v(-15, -108) * mm, "end": v(-33, -90) * mm});
            skLineSegment(sketch, "E97.0", {"start": v(-70, 90) * mm, "end": v(70, 90) * mm});
            skLineSegment(sketch, "E98.0", {"start": v(-80, -80) * mm, "end": v(-80, 80) * mm});
            skLineSegment(sketch, "E99.0", {"start": v(-70, -90) * mm, "end": v(70, -90) * mm});
            skLineSegment(sketch, "E100.0", {"start": v(80, -80) * mm, "end": v(80, 80) * mm});
            skArc(sketch, "E101.0", {"start": v(80, 80) * mm, "mid": v(77.07, 87.07) * mm, "end": v(70, 90) * mm});
            skArc(sketch, "E102.0", {"start": v(70, -90) * mm, "mid": v(77.07, -87.07) * mm, "end": v(80, -80) * mm});
            skArc(sketch, "E103.0", {"start": v(-80, -80) * mm, "mid": v(-77.07, -87.07) * mm, "end": v(-70, -90) * mm});
            skArc(sketch, "E104.0", {"start": v(56.15, 48.18) * mm, "mid": v(0, 67.5) * mm, "end": v(-56.15, 48.18) * mm});
            skArc(sketch, "E105.0", {"start": v(60, 40.3) * mm, "mid": v(58.99, 44.68) * mm, "end": v(56.15, 48.18) * mm});
            skLineSegment(sketch, "E106.0", {"start": v(60, 40.3) * mm, "end": v(60, -40.3) * mm});
            skArc(sketch, "E107.0", {"start": v(56.15, -48.18) * mm, "mid": v(58.99, -44.68) * mm, "end": v(60, -40.3) * mm});
            skArc(sketch, "E108.0", {"start": v(-56.15, -48.18) * mm, "mid": v(0, -67.5) * mm, "end": v(56.15, -48.18) * mm});
            skArc(sketch, "E109.0", {"start": v(-60, -40.3) * mm, "mid": v(-58.99, -44.68) * mm, "end": v(-56.15, -48.18) * mm});
            skLineSegment(sketch, "E110.0", {"start": v(-60, 40.3) * mm, "end": v(-60, -40.3) * mm});
            skArc(sketch, "E111.0", {"start": v(-56.15, 48.18) * mm, "mid": v(-58.99, 44.68) * mm, "end": v(-60, 40.3) * mm});
            skCircle(sketch, "E112.0", {"center": v(-60, 67.5) * mm, "radius": 4 * mm});
            skCircle(sketch, "E113.0", {"center": v(60, 67.5) * mm, "radius": 4 * mm});
            skCircle(sketch, "E114.0", {"center": v(60, -67.5) * mm, "radius": 4 * mm});
            skCircle(sketch, "E115.0", {"center": v(-60, -67.5) * mm, "radius": 4 * mm});
            skSolve(sketch);
        }
        {
            var Q0;
            Q0=makeQuery(id+"F16.imprint","IMPRINT",FACE,{"disambiguationData":[TD([[makeQuery(id+"F16.imprint","IMPRINT",EDGE,{"derivedFrom":sQuery(id+"F16.wireOp",EDGE,"E98.0")}),-1.0]])]});
            var Q1;
            Q1=makeQuery(id+"F16.imprint","IMPRINT",FACE,{"disambiguationData":[TD([[makeQuery(id+"F16.imprint","IMPRINT",EDGE,{"derivedFrom":sQuery(id+"F16.wireOp",EDGE,"E80")}),-1.0]])]});
            var Q2;
            Q2=makeQuery(id+"F16.imprint","IMPRINT",FACE,{"disambiguationData":[TD([[makeQuery(id+"F16.imprint","IMPRINT",EDGE,{"derivedFrom":sQuery(id+"F16.wireOp",EDGE,"E82")}),-1.0]])]});
            var Q3;
            Q3=makeQuery(id+"F2.opExtrude","CAP_FACE",FACE,{"disambiguationData":[OSD([sQuery(id+"F0.wireOp",EDGE,"E12"),sQuery(id+"F0.wireOp",EDGE,"E13"),sQuery(id+"F0.wireOp",EDGE,"E14"),sQuery(id+"F0.wireOp",EDGE,"E15"),sQuery(id+"F0.wireOp",EDGE,"E17.filletArc"),sQuery(id+"F0.wireOp",EDGE,"E18.filletArc"),sQuery(id+"F0.wireOp",EDGE,"E19.filletArc"),sQuery(id+"F0.wireOp",EDGE,"E20.filletArc"),sQuery(id+"F0.wireOp",EDGE,"E25.0"),sQuery(id+"F0.wireOp",EDGE,"E25.1"),sQuery(id+"F0.wireOp",EDGE,"E25.2"),sQuery(id+"F0.wireOp",EDGE,"E25.3"),sQuery(id+"F0.wireOp",EDGE,"E25.4"),sQuery(id+"F0.wireOp",EDGE,"E25.5"),sQuery(id+"F0.wireOp",EDGE,"E25.6"),sQuery(id+"F0.wireOp",EDGE,"E25.7")])],"isStart":false});
            extrude(context, id + "F17", {"entities" : qUnion([Q0, Q1, Q2]), "endBound" : BoundingType.UP_TO_SURFACE, "endBoundEntityFace" : qUnion([Q3]), "depth" : 25 * mm});
        }
    });
